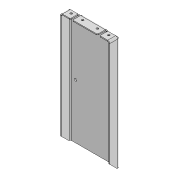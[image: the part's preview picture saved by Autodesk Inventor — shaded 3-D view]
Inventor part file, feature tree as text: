
AUTODESK INVENTOR PART (.ipt)
format: ipt  version: 2020 (Build 240168000, 168)  size: 199,168 bytes
history: native  units: mm
features: other x14, sketch x7, hole x2, extrude x1, chamfer x1, fillet x1
ambient origin geometry x8: Origin, YZ Plane, XZ Plane, XY Plane, X Axis, Y Axis, Z Axis, Center Point
bodies: Body1 (feature_tree)
feature tree (26):
  other  "ソリッド1"
  other  "フランジ1"
  other  "フランジ5"
  extrude  "押し出し1"  Depth=100.0mm
  other  "フランジ6"
  hole  "穴1"  [1 undecoded]
  chamfer  "面取り1"  Distance=227.0mm
  hole  "穴2"  [1 undecoded]
  fillet  "フィレット1"  Radius=2.0mm
  sketch  "スケッチ1"
  other  "プレート1"
  sketch  "スケッチ2"
  other  "プレート2"
  other  "曲げ1"
  other  "コーナー1"
  sketch  "スケッチ6"
  other  "プレート6"
  other  "曲げ5"
  other  "コーナー5"
  sketch  "スケッチ7"
  sketch  "スケッチ8"
  other  "プレート7"
  other  "曲げ6"
  other  "コーナー6"
  sketch  "スケッチ9"
  sketch  "スケッチ10"
note: 2 required parameter values undecoded (feature->parameter linkage not recoverable at this tier; creation-order binding heuristic only, values carry confidence <= 0.55)
